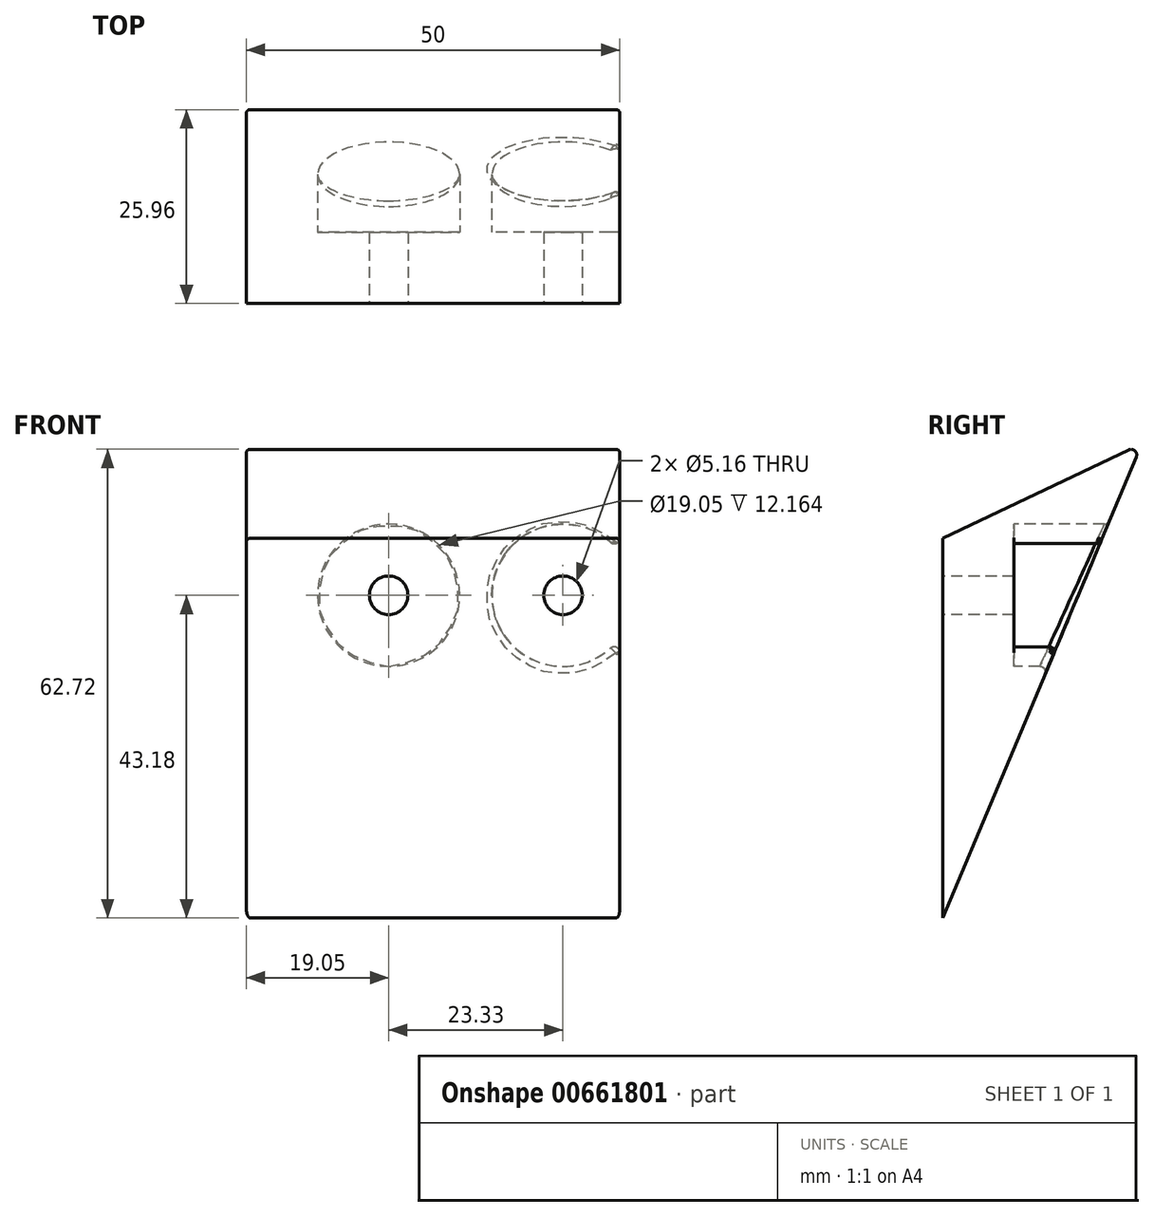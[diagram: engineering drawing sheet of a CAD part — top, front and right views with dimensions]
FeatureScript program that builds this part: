
annotation { "Feature Type Name" : "Feature", "Feature Type Description" : "" }
export const myFeature = defineFeature(function(context is Context, id is Id, definition is map)
    precondition{}
    {
        {
            var Q0;
            Q0=qCreatedBy(makeId("Right.planeOp"),FACE);
            var sketch = newSketch(context, id + "F0", { "sketchPlane" : qUnion([Q0])});
            skLineSegment(sketch, "E0.bottom", {"start": v(-22.12, -25.4) * mm, "end": v(22.12, -25.4) * mm, "construction": true});
            skLineSegment(sketch, "E0.top", {"start": v(-22.12, 25.4) * mm, "end": v(22.12, 25.4) * mm, "construction": true});
            skLineSegment(sketch, "E0.left", {"start": v(-22.12, -25.4) * mm, "end": v(-22.12, 25.4) * mm, "construction": true});
            skLineSegment(sketch, "E0.right", {"start": v(22.12, -25.4) * mm, "end": v(22.12, 25.4) * mm});
            skPoint(sketch, "E0.middle", {"position": v(0, 0) * mm});
            skLineSegment(sketch, "E1", {"start": v(22.12, 25.4) * mm, "end": v(48.8, 38.1) * mm});
            skLineSegment(sketch, "E2", {"start": v(48.8, 38.1) * mm, "end": v(22.12, -25.4) * mm});
            skSolve(sketch);
        }
        {
            var Q0;
            {var subQ0=sQuery(id+"F0.wireOp",EDGE,"E0.right");Q0=makeQuery(id+"F0.imprint","IMPRINT",FACE,{"disambiguationData":[TD([[makeQuery(id+"F0.imprint","IMPRINT",EDGE,{"derivedFrom":subQ0}),-1.0]])]});}
            var Q1;
            {var subQ0=sQuery(id+"F0.wireOp",EDGE,"E1");Q1=makeQuery(id+"F0.imprint","IMPRINT",FACE,{"disambiguationData":[TD([[makeQuery(id+"F0.imprint","IMPRINT",EDGE,{"derivedFrom":subQ0}),-1.0]])]});}
            extrude(context, id + "F1", {"entities" : qUnion([Q0, Q1]), "depth" : 50 * mm, "offsetDistance" : 25.4 * mm});
        }
        {
            var Q0;
            Q0=makeQuery(id+"F1.opExtrude","SWEPT_FACE",FACE,{"disambiguationData":[OSD([sQuery(id+"F0.wireOp",EDGE,"E0.right")])]});
            cPlane(context, id + "F2", {"entities" : qUnion([Q0]), "cplaneType" : CPlaneType.OFFSET, "offset" : 9.52 * mm, "oppositeDirection" : true, "width" : 152.4 * mm, "height" : 152.4 * mm});
        }
        {
            var Q0;
            Q0=qCreatedBy(id+"F2.planeOp",FACE);
            var sketch = newSketch(context, id + "F3", { "sketchPlane" : qUnion([Q0])});
            skLineSegment(sketch, "E3.0", {"start": v(50, 25.4) * mm, "end": v(0, 25.4) * mm});
            skCircle(sketch, "E4", {"center": v(42.38, 17.78) * mm, "radius": 2.58 * mm});
            skCircle(sketch, "E5", {"center": v(19.05, 17.78) * mm, "radius": 2.58 * mm});
            skLineSegment(sketch, "E6.0", {"start": v(50, -25.4) * mm, "end": v(50, 25.4) * mm});
            skSolve(sketch);
        }
        {
            var Q0;
            Q0=qSketchRegion(id+"F3",true);
            extrude(context, id + "F4", {"entities" : qUnion([Q0]), "operationType" : NewBodyOperationType.REMOVE, "endBound" : BoundingType.THROUGH_ALL, "oppositeDirection" : true, "depth" : 25.4 * mm, "offsetDistance" : 25.4 * mm, "hasSecondDirection" : true, "secondDirectionBound" : SecondDirectionBoundingType.THROUGH_ALL, "secondDirectionOppositeDirection" : false, "secondDirectionDepth" : 25.4 * mm});
        }
        {
            var Q0;
            Q0=qCreatedBy(id+"F2.planeOp",FACE);
            var sketch = newSketch(context, id + "F5", { "sketchPlane" : qUnion([Q0])});
            skCircle(sketch, "E7.0", {"center": v(42.38, 17.78) * mm, "radius": 2.58 * mm});
            skCircle(sketch, "E8.0", {"center": v(19.05, 17.78) * mm, "radius": 2.58 * mm});
            skCircle(sketch, "E9", {"center": v(42.38, 17.78) * mm, "radius": 9.53 * mm});
            skCircle(sketch, "E10", {"center": v(19.05, 17.78) * mm, "radius": 9.53 * mm});
            skLineSegment(sketch, "E11.0", {"start": v(50, 38.1) * mm, "end": v(50, -25.4) * mm});
            skSolve(sketch);
        }
        {
            var Q0;
            Q0=qSketchRegion(id+"F5",true);
            extrude(context, id + "F6", {"entities" : qUnion([Q0]), "operationType" : NewBodyOperationType.REMOVE, "oppositeDirection" : true, "depth" : 25.4 * mm, "offsetDistance" : 25.4 * mm});
        }
        {
            var Q0;
            Q0=makeQuery(id+"F1.opExtrude","SWEPT_EDGE",EDGE,{"disambiguationData":[OSD([sQuery(id+"F0.wireOp",EDGE,"E1"),sQuery(id+"F0.wireOp",EDGE,"E2")])]});
            fillet(context, id + "F7", {"entities" : qUnion([Q0]), "radius" : 0.76 * mm, "tangentPropagation" : true, "allowEdgeOverflow" : false});
        }
        {
            var Q0;
            Q0=makeQuery(id+"F1.opExtrude","CAP_EDGE",EDGE,{"disambiguationData":[OSD([sQuery(id+"F0.wireOp",EDGE,"E2")])],"isStart":true});
            fillet(context, id + "F8", {"entities" : qUnion([Q0]), "radius" : 0.5 * mm, "tangentPropagation" : true, "allowEdgeOverflow" : false});
        }
        {
            var Q0;
            {var subQ0=sQuery(id+"F0.wireOp",EDGE,"E2");var subQ1=sQuery(id+"F0.wireOp",EDGE,"E1");Q0=makeQuery(id+"F6.boolean.opBoolean","SPLIT",EDGE,{"disambiguationData":[TD([makeQuery(id+"F1.opExtrude","SWEPT_FACE",FACE,{"disambiguationData":[OSD([subQ1])]})])],"derivedFrom":makeQuery(id+"F1.opExtrude","CAP_EDGE",EDGE,{"disambiguationData":[OSD([subQ0])],"isStart":false})});}
            var Q1;
            {var subQ0=sQuery(id+"F0.wireOp",EDGE,"E0.right");var subQ1=sQuery(id+"F0.wireOp",EDGE,"E2");Q1=makeQuery(id+"F6.boolean.opBoolean","SPLIT",EDGE,{"disambiguationData":[TD([makeQuery(id+"F1.opExtrude","SWEPT_FACE",FACE,{"disambiguationData":[OSD([subQ0])]})])],"derivedFrom":makeQuery(id+"F1.opExtrude","CAP_EDGE",EDGE,{"disambiguationData":[OSD([subQ1])],"isStart":false})});}
            fillet(context, id + "F9", {"entities" : qUnion([Q0, Q1]), "radius" : 0.5 * mm, "tangentPropagation" : true, "allowEdgeOverflow" : false});
        }
        {
            var Q0;
            Q0=makeQuery(id+"F6.boolean.opBoolean","INTERSECT",EDGE,{"derivedFrom":[makeQuery(id+"F1.opExtrude","SWEPT_FACE",FACE,{"disambiguationData":[OSD([sQuery(id+"F0.wireOp",EDGE,"E2")])]}),makeQuery(id+"F6.opExtrude","SWEPT_FACE",FACE,{"disambiguationData":[OSD([sQuery(id+"F5.wireOp",EDGE,"E10")])]})]});
            var Q1;
            Q1=makeQuery(id+"F6.boolean.opBoolean","INTERSECT",EDGE,{"derivedFrom":[makeQuery(id+"F1.opExtrude","SWEPT_FACE",FACE,{"disambiguationData":[OSD([sQuery(id+"F0.wireOp",EDGE,"E2")])]}),makeQuery(id+"F6.opExtrude","SWEPT_FACE",FACE,{"disambiguationData":[OSD([sQuery(id+"F5.wireOp",EDGE,"E9")])]})]});
            fillet(context, id + "F10", {"entities" : qUnion([Q0, Q1]), "radius" : 0.76 * mm, "tangentPropagation" : true, "allowEdgeOverflow" : false});
        }
    });
